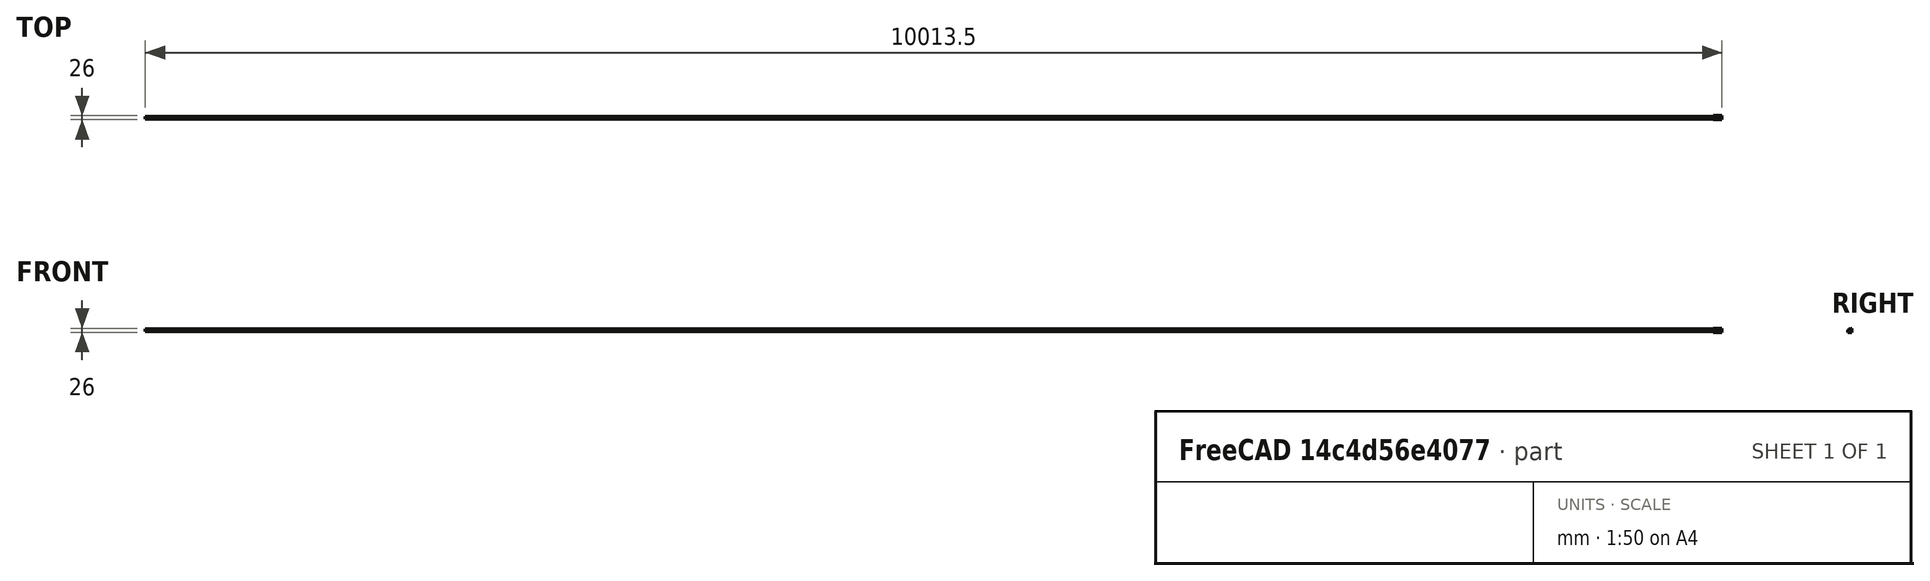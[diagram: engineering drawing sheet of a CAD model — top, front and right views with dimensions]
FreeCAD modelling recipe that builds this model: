
FCSTD DOCUMENT  (FreeCAD 0.16R6704 (Git))
Label: proj1
License: All rights reserved
LicenseURL: http://en.wikipedia.org/wiki/All_rights_reserved
objects: Sketcher::SketchObject×5, PartDesign::Pad×3, PartDesign::Pocket×2, PartDesign::Mirrored×2, Mesh::Feature×1
note: 17 computed .brp shape members not serialized (recipe doc carries the construction recipe); baked Part::Feature solids carry a one-line shape summary decoded from their .brp

FEATURE [Sketcher::SketchObject] Sketch
  Placement = pos=(0,0,0) rot=(0.57735,0.57735,0.57735;2.0944rad)
  sketch-geometry (4):
    g0: LineSegment StartX=-13 StartY=-13 StartZ=0 EndX=13 EndY=-13 EndZ=0
    g1: LineSegment StartX=13 StartY=-13 StartZ=0 EndX=13 EndY=13 EndZ=0
    g2: LineSegment StartX=13 StartY=13 StartZ=0 EndX=8 EndY=13 EndZ=0
    g3: LineSegment StartX=8 StartY=13 StartZ=0 EndX=-13 EndY=-13 EndZ=0
  constraints (11):
    c: Horizontal(g0)
    c: Coincident(g0,g1)
    c: Vertical(g1)
    c: Coincident(g1,g2)
    c: Coincident(g2,g3)
    c: Coincident(g3,g0)
    c: Equal(g0,g1)
    c: Horizontal(g2)
    c: Symmetric(g1,g0,g-1)
    c: DistanceX(g2,g2) = 5
    c: DistanceY(g1,g1) = 26
FEATURE [PartDesign::Pad] Pad
  Length = 53
  Length2 = 100
  Midplane = true
  Placement = pos=(0,0,0) rot=(0.57735,0.57735,0.57735;2.0944rad)
  Sketch = -> Sketch
  Type = 0
FEATURE [Sketcher::SketchObject] Sketch001
  ExternalGeometry = -> [Pad]
  Placement = pos=(0,13,0) rot=(0.57735,0.57735,0.57735;4.18879rad)
  Support = -> Pad [Face2]
  sketch-geometry (4):
    g0: LineSegment StartX=8 StartY=26.5 StartZ=0 EndX=13 EndY=26.5 EndZ=0
    g1: LineSegment StartX=13 StartY=26.5 StartZ=0 EndX=13 EndY=15.5 EndZ=0
    g2: LineSegment StartX=13 StartY=15.5 StartZ=0 EndX=8 EndY=15.5 EndZ=0
    g3: LineSegment StartX=8 StartY=15.5 StartZ=0 EndX=8 EndY=26.5 EndZ=0
  constraints (11):
    c: Coincident(g0,g1)
    c: Coincident(g1,g2)
    c: Coincident(g2,g3)
    c: Coincident(g3,g0)
    c: Horizontal(g0)
    c: Horizontal(g2)
    c: Vertical(g1)
    c: Vertical(g3)
    c: DistanceX(g0,g0) = 5
    c: DistanceY(g3,g3) = 11
    c: Coincident(g-3,g0)
FEATURE [PartDesign::Pocket] Pocket
  Length = 5
  Placement = pos=(0,0,0) rot=(0.57735,0.57735,0.57735;2.0944rad)
  Sketch = -> Sketch001
  Type = 1
FEATURE [PartDesign::Mirrored] Mirrored
  MirrorPlane = -> Sketch001 [H_Axis]
  Originals = -> [Pocket]
  Placement = pos=(0,0,0) rot=(0.57735,0.57735,0.57735;2.0944rad)
FEATURE [Sketcher::SketchObject] Sketch002
  ExternalGeometry = -> [Mirrored]
  Placement = pos=(0,13,0) rot=(0.57735,0.57735,0.57735;4.18879rad)
  Support = -> Mirrored [Face3]
  sketch-geometry (4):
    g0: LineSegment StartX=-13 StartY=26.5 StartZ=0 EndX=3.7 EndY=26.5 EndZ=0
    g1: LineSegment StartX=3.7 StartY=26.5 StartZ=0 EndX=3.7 EndY=19.5 EndZ=0
    g2: LineSegment StartX=3.7 StartY=19.5 StartZ=0 EndX=-13 EndY=19.5 EndZ=0
    g3: LineSegment StartX=-13 StartY=19.5 StartZ=0 EndX=-13 EndY=26.5 EndZ=0
  constraints (11):
    c: Coincident(g0,g1)
    c: Coincident(g1,g2)
    c: Coincident(g2,g3)
    c: Coincident(g3,g0)
    c: Horizontal(g0)
    c: Horizontal(g2)
    c: Vertical(g1)
    c: Vertical(g3)
    c: DistanceX(g0,g0) = 16.7
    c: DistanceY(g1,g1) = 7
    c: Coincident(g-3,g0)
FEATURE [PartDesign::Pad] Pad001
  Length = 26
  Length2 = 100
  Placement = pos=(0,0,0) rot=(0.57735,0.57735,0.57735;2.0944rad)
  Reversed = true
  Sketch = -> Sketch002
  Type = 0
FEATURE [PartDesign::Mirrored] Mirrored001
  MirrorPlane = -> Sketch002 [H_Axis]
  Originals = -> [Pad001]
  Placement = pos=(0,0,0) rot=(0.57735,0.57735,0.57735;2.0944rad)
FEATURE [Sketcher::SketchObject] Sketch003
  ExternalGeometry = -> [Mirrored001]
  Placement = pos=(0,-1.51298,1.22202) rot=(0.395866,0.395866,-0.828601;1.75771rad)
  Support = -> Mirrored001 [Face4]
  sketch-geometry (4):
    g0: LineSegment StartX=-5.71838 StartY=8.5 StartZ=0 EndX=11.2816 EndY=8.5 EndZ=0
    g1: LineSegment StartX=11.2816 StartY=8.5 StartZ=0 EndX=11.2816 EndY=-8.5 EndZ=0
    g2: LineSegment StartX=11.2816 StartY=-8.5 StartZ=0 EndX=-5.71838 EndY=-8.5 EndZ=0
    g3: LineSegment StartX=-5.71838 StartY=-8.5 StartZ=0 EndX=-5.71838 EndY=8.5 EndZ=0
  constraints (12):
    c: Coincident(g0,g1)
    c: Coincident(g1,g2)
    c: Coincident(g2,g3)
    c: Coincident(g3,g0)
    c: Horizontal(g0)
    c: Horizontal(g2)
    c: Vertical(g1)
    c: Vertical(g3)
    c: DistanceY(g3,g3) = 17
    c: DistanceX(g0,g0) = 17
    c: DistanceX(g0,g-3) = 7
    c: DistanceY(g0,g-3) = 11
FEATURE [PartDesign::Pad] Pad002
  Length = 1
  Length2 = 100
  Placement = pos=(0,0,0) rot=(0.57735,0.57735,0.57735;2.0944rad)
  Sketch = -> Sketch003
  Type = 0
FEATURE [Sketcher::SketchObject] Sketch004
  ExternalGeometry = -> [Pad002]
  Placement = pos=(0,13,0) rot=(0.57735,0.57735,0.57735;4.18879rad)
  Support = -> Pad002 [Face2]
  sketch-geometry (4):
    g0: LineSegment StartX=-7.55441 StartY=8.5 StartZ=0 EndX=5.67059 EndY=8.5 EndZ=0
    g1: LineSegment StartX=5.67059 StartY=8.5 StartZ=0 EndX=5.67059 EndY=-8.5 EndZ=0
    g2: LineSegment StartX=5.67059 StartY=-8.5 StartZ=0 EndX=-7.55441 EndY=-8.5 EndZ=0
    g3: LineSegment StartX=-7.55441 StartY=-8.5 StartZ=0 EndX=-7.55441 EndY=8.5 EndZ=0
  constraints (10):
    c: Coincident(g0,g1)
    c: Coincident(g1,g2)
    c: Coincident(g2,g3)
    c: Coincident(g3,g0)
    c: Horizontal(g0)
    c: Horizontal(g2)
    c: Vertical(g1)
    c: Vertical(g3)
    c: Coincident(g0,g-6)
    c: Coincident(g2,g-5)
FEATURE [PartDesign::Pocket] Pocket001
  Length = 5
  Placement = pos=(0,0,0) rot=(0.57735,0.57735,0.57735;2.0944rad)
  Sketch = -> Sketch004
  Type = 1
FEATURE [Mesh::Feature] Mesh  label="Pocket001 (Meshed)"
